# Revit family: 1404a_omni_bp_ir
name_source: partatom
category: Communication Devices
units: mm (PartAtom-declared; Revit-internal decimal feet)

## family parameters
Cut with Voids When Loaded = No
Host = Face
Maintain Annotation Orientation = No
OmniClass Number = 23.85.80.11.27
OmniClass Title = Lighting Controls
Part Type = Normal
Room Calculation Point = No
Round Connector Dimension = Use Diameter
Shared = Yes

## types (1)
- 1404a_omni_bp_ir
    Assembly Code = D5090
    Certifications = UL and cUL listed
    Coverage = 450 square foot
    Default Elevation = 48 "
    Description = The OMNIDIABP line voltage ceiling sensor combines passive infrared (PIR) and
acoustic (sound-activated) technologies to turn lighting systems on and off based
on occupancy. The OMNIDIABP features Controls' patented IntelliDAPT®
technology, which makes all the sensor adjustments automatically.
    Features = IntelliDAPT self-adaptive technology—no manual adjustment required 
All-digital dual technology (acoustic and passive infrared [PIR]) sensor 
Non-volatile memory for sensor settings 
450 square-foot coverage 
Self-contained power supply
Universal voltage (120-277VAC; 50/60 Hz) 
UL and cUL listed 
California Title 24 compliant 
Five-year warranty 
120-277 Vac
    Housing Material = Paint -  Matte White
    Manufacturer = NX Lighting Controls
    Model = OMNI®-BPLine Voltage Dual Technology Acoustic and Passive Infrared
    Sensing Element = Paint -  Matte White
    Type Comments = CEILING MOUNT OCCUPANCY SENSORS
    URL = https://www.currentlighting.com
    Warranty = 5-Years Warranty
    Width = 4.5 "

## geometry (parser evidence)
native form markers: Sweep x3
no freeform markers — native parametric forms only
